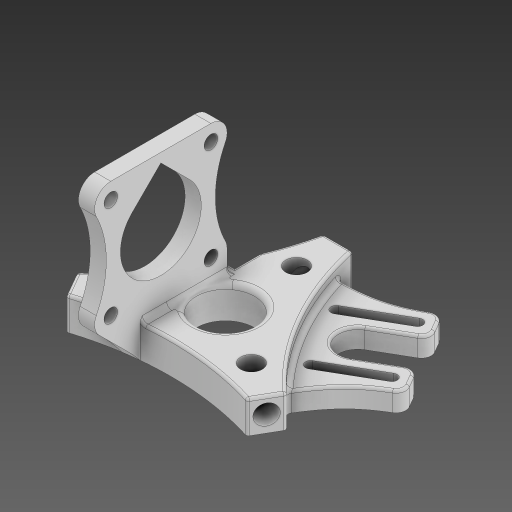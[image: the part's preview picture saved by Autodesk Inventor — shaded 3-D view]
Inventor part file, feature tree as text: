
AUTODESK INVENTOR PART (.ipt)
format: ipt  version: 2024 (Build 280153000, 153)  size: 598,016 bytes
history: native  units: mm
features: fillet x8, sketch x6, extrude x5, hole x3, plane x2, pattern_circular x1, projected_geometry x1
ambient origin geometry x8: Origin, YZ Plane, XZ Plane, XY Plane, X Axis, Y Axis, Z Axis, Center Point
bodies: Body1 (feature_tree)
feature tree (26):
  extrude  "Extrusion2"  Depth=6.65mm
  plane  "Work Plane3"
  sketch  "Sketch6"  dims[d14=30.0deg d15=30.0deg]
  extrude  "Extrusion3"  TaperAngle=30.0deg  [1 undecoded]
  hole  "Hole2"  [1 undecoded]
  plane  "Work Plane4"
  extrude  "Extrusion4"  Depth=17.0mm
  fillet  "Fillet1"  Radius=30.0mm
  fillet  "Fillet3"  Radius=10.0mm
  fillet  "Fillet8"  [1 undecoded]
  fillet  "Fillet9"  Radius=11.0mm
  fillet  "Fillet11"  Radius=22.0mm
  hole  "Hole5"  [1 undecoded]
  pattern_circular  "Circular Pattern2"  [2 undecoded]
  fillet  "Fillet13"  Radius=10.0mm
  sketch  "Sketch12"  dims[d44=25.0mm d45=31.0mm]
  extrude  "Extrusion5"  Depth=20.0mm
  extrude  "Extrusion6"  Depth=30.0mm
  hole  "Hole6"  [1 undecoded]
  fillet  "Fillet14"  Radius=5.0mm
  fillet  "Fillet15"  [1 undecoded]
  sketch  "Sketch2"  dims[d9=18.0mm d10=6.65mm]
  sketch  "Sketch8"  dims[d22=17.0mm d23=22.0mm]
  sketch  "Sketch11"  dims[d24=6.0mm d27=17.0mm d28=30.0mm d30=360.0deg d32=10.0mm d33=0.0mm d41=-9.0mm d42=11.0mm d43=22.0mm]
  sketch  "Sketch13"  dims[d46=31.0mm d48=5.0mm d49=10.0mm d50=20.0mm d52=31.0mm d53=20.0mm d55=31.0mm d58=30.0mm d60=30.0mm d61=5.0mm d62=0.0mm d70=4.2mm d71=6.0mm d72=8.2mm d73=2.0mm d74=90.0deg d75=8.0mm d76=0.0mm d77=-10.0mm d78=17.0mm d79=28.0mm d80=30.94mm d81=4.372mm d82=18.4mm d83=4.662mm d84=4.662mm d85=3.23mm d86=3.23mm d88=9.5mm d89=9.5mm d90=15.0mm d91=6.0mm d92=0.0mm d93=3.0mm d95=0.75mm d100=1.6mm d101=0.75mm d114=6.0mm d116=30.0mm d118=360.0deg d120=37.0mm d128=9.0mm d129=6.2mm d130=6.0mm d131=4.0mm d132=2.0mm d133=90.0deg d134=12.0mm d135=0.0mm d136=5.0mm d137=30.0mm d138=360.0deg d141=1.5mm d142=45.0deg d143=12.9mm d144=15.0mm d145=10.0mm d146=9.15mm d147=2.0mm d148=2.0mm d149=10.0mm d150=0.0mm d151=0.0mm d152=0.0mm d153=3.5mm d154=6.0mm d155=3.023mm d156=2.0mm d157=14.3117mm d158=15.0mm d159=0.0mm d160=3.1mm d161=5.0mm d162=6.5mm d163=0.8mm d164=11.0mm]
  projected_geometry  "Project Cut Edges1"
note: 8 required parameter values undecoded (feature->parameter linkage not recoverable at this tier; creation-order binding heuristic only, values carry confidence <= 0.55)
